# Revit family: Shower_System-Delta-Trinsic
name_source: partatom
category: Plumbing Fixtures
revit_build: Autodesk Revit MEP 2012 (Build: 20110916_2132(x64)
units: mm (PartAtom-declared; Revit-internal decimal feet)

## types (4) — shared parameters
Date Modified = July 17, 2015
Default Elevation = 48 "
Depth = 12.087 "
Equipment Abbreviation = SS
Family Version = 1.0
Height = 30.485 "
Manufacturer = Delta Faucet Company
Model Disclaimer = Contact Delta Faucet Company for More Information
Product Documentation Link = http://www.deltafaucet.com
Product Page URL = http://www.deltafaucet.com
URL = http://www.deltafaucet.com
Width = 6.435 "

## per-type parameters (varying)
| type | Description | Model | Product Material | z Spout Family | z Type | z Type Spout | z Valve Family |
| Chrome, Curved Spout | Trinsic Shower System, Curved Tub Spout, Chrome | 17T459 | Chrome - Delta - Polished | Spout459 : Standard | 1 | 1 | Valve459 : Standard |
| Stainless Steel, Straight Spout | Trinsic Shower System, Curved Tub Spout, Stainless | 17T461-SS | Stainless Steel - Delta - Polished | Spout461 : Standard | 2 | 2 | Valve461 : Standard |
| Chrome, Straight Spout | Trinsic Shower System, Straight Tub Spout, Chrome | 17T461 | Chrome - Delta - Polished | Spout461 : Standard | 1 | 2 | Valve461 : Standard |
| Stainless Steel, Curved Spout | Trinsic Shower System, Curved Tub Spout, Stainless | 17T459-SS | Stainless Steel - Delta - Polished | Spout459 : Standard | 2 | 1 | Valve459 : Standard |

## geometry (parser evidence)
native form markers: Blend x4, Sweep x13
no freeform markers — native parametric forms only
